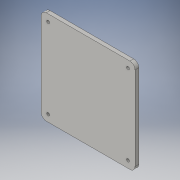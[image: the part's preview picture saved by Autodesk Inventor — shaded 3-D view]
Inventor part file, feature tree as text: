
AUTODESK INVENTOR PART (.ipt)
format: ipt  version: 2016 (Build 200138000, 138)  size: 109,568 bytes
history: native  units: in
note: dims shown in document units (in); Inventor stores cm internally (conversion verified against a paired STEP export)
features: extrude x1, fillet x1, sketch x1
ambient origin geometry x8: Origin, YZ Plane, XZ Plane, XY Plane, X Axis, Y Axis, Z Axis, Center Point
bodies: Solid1 (feature_tree)
feature tree (3):
  extrude  "Extrusion1"  Depth=4.625in
  fillet  "Fillet1"  Radius=0.145in
  sketch  "Sketch1"  dims[d0=4.625in d1=4.625in d2=0.145in d7=0.145in d11=0.145in d13=0.1875in d14=0.0in d15=0.25in d29=3.937in d30=3.937in d31=3.937in d32=0.145in]
